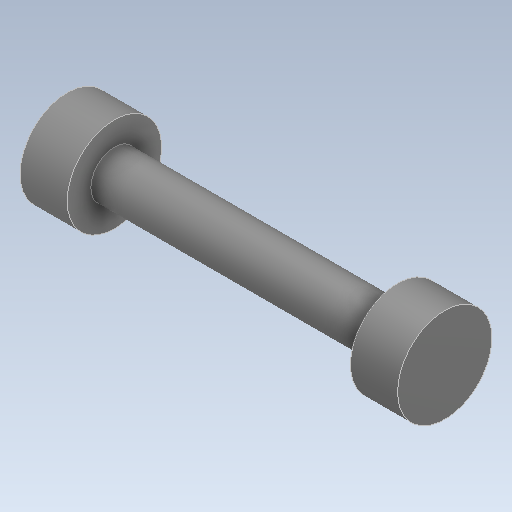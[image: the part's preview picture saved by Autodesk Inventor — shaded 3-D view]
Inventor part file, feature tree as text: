
AUTODESK INVENTOR PART (.ipt)
format: ipt  version: 2021 (Build 250183000, 183)  size: 114,688 bytes
history: mixed  units: mm
features: other x1, revolve x1, imported_body x1
ambient origin geometry x8: Origin, YZ Plane, XZ Plane, XY Plane, X Axis, Y Axis, Z Axis, Center Point
bodies: Body1 (imported_parasolid)
feature tree (3):
  other  "Sólido1"
  revolve  "Revolución1"  [1 undecoded]
  imported_body  NMx_Import_Brep_tag  [imported B-rep: ~7 faces, bbox_mm=[40.0, 0.0, 2.5]]
note: 1 required parameter value undecoded (feature->parameter linkage not recoverable at this tier; creation-order binding heuristic only, values carry confidence <= 0.55)
